# Revit family: Robuust Basic
name_source: partatom
category: Mechanical Equipment
units: mm (PartAtom-declared; Revit-internal decimal feet)

## family parameters
Always vertical = Yes
Cut with Voids When Loaded = No
Host = Wall
OmniClass Number = 23.75.00.00
OmniClass Title = Climate Control (HVAC)
Part Type = Normal
Room Calculation Point = No
Round Connector Dimension = Use Diameter
Shared = No

## types (5) — shared parameters
Manufacturer = Masterwatt B.V.
URL = https://masterwatt.nl
Voltage = 230 V
zero-valued in all types: Default Elevation

## per-type parameters (varying)
| type | 1000B | 1500B | 2000B | 2500B | 500B | Art. No. | Model | Watt |
| 0500 B | No | No | No | No | Yes | 429 752 100 | Robuust-500B | 500 VA |
| 1000 B | No | Yes | No | No | No | 429 752 102 | Robuust-1000B | 1000 VA |
| 1500 B | No | No | Yes | No | No | 429 752 104 | Robuust-1500B | 1500 VA |
| 2000 B | No | No | No | Yes | No | 429 752 106 | Robuust-2000B | 2000 VA |
| 2500 B | Yes | No | No | No | No | 429 752 107 | Robuust-2500B | 2500 VA |

## geometry (parser evidence)
native form markers: Sweep x38
no freeform markers — native parametric forms only
